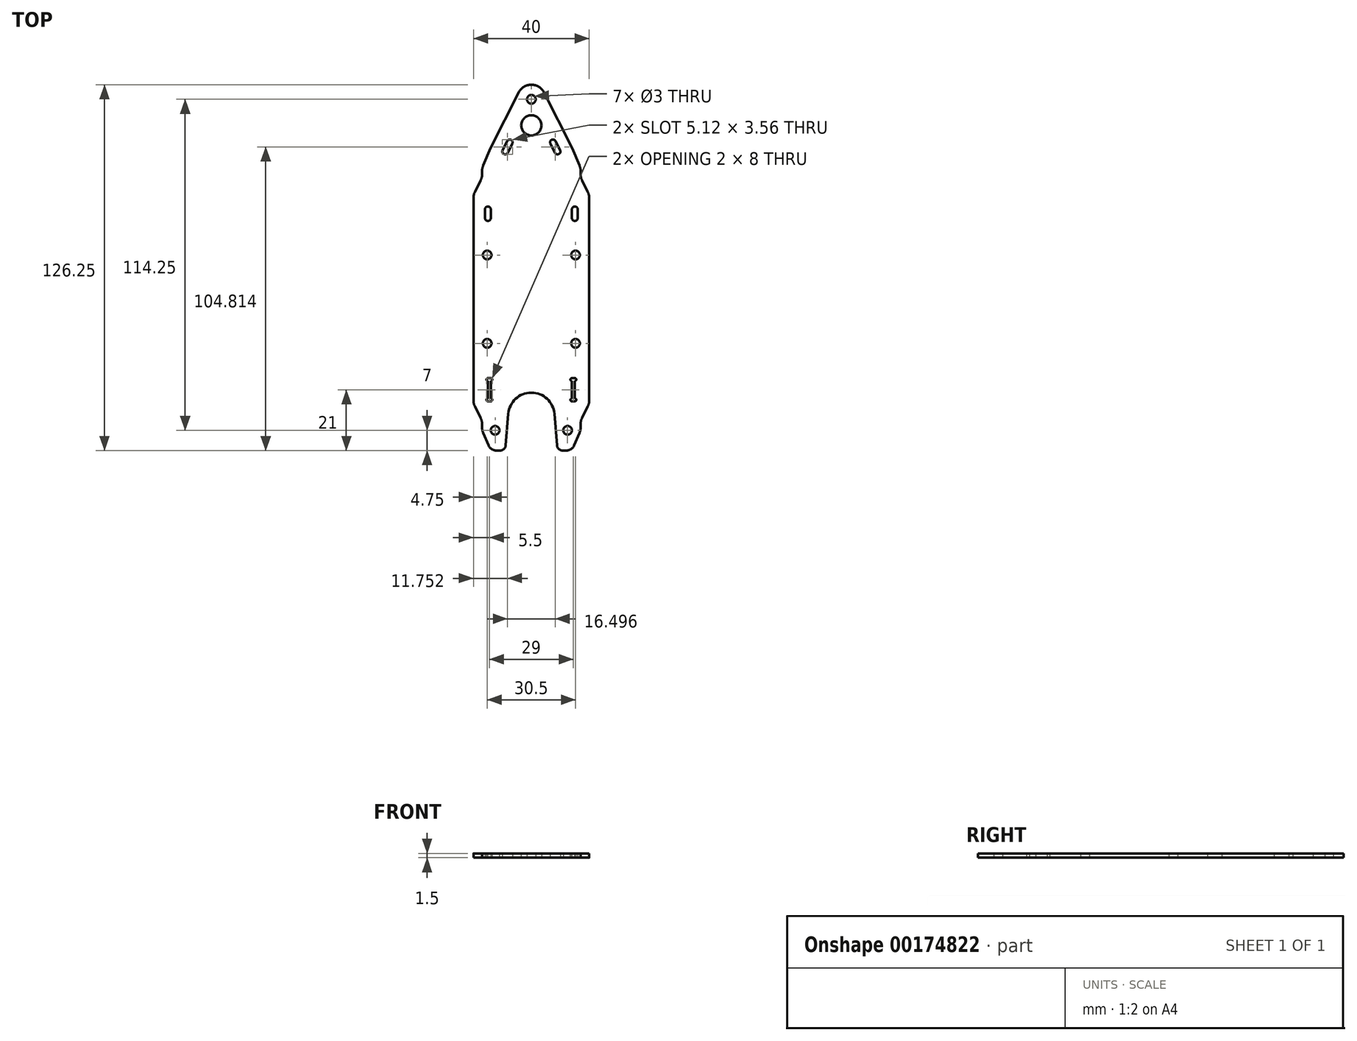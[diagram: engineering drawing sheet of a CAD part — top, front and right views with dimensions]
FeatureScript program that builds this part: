
annotation { "Feature Type Name" : "Feature", "Feature Type Description" : "" }
export const myFeature = defineFeature(function(context is Context, id is Id, definition is map)
    precondition{}
    {
        {
            var Q0;
            Q0=qCreatedBy(makeId("Top.planeOp"),FACE);
            var sketch = newSketch(context, id + "F0", { "sketchPlane" : qUnion([Q0])});
            skLineSegment(sketch, "E0.left", {"start": v(-20, 36) * mm, "end": v(-20, -36) * mm});
            skLineSegment(sketch, "E0.right", {"start": v(20, 36) * mm, "end": v(20, -36) * mm});
            skLineSegment(sketch, "E1.left", {"start": v(-17, 45.25) * mm, "end": v(-17, 42) * mm});
            skLineSegment(sketch, "E1.right", {"start": v(17, 45.25) * mm, "end": v(17, 42) * mm});
            skLineSegment(sketch, "E2.top", {"start": v(-14, -52.25) * mm, "end": v(-9, -52.25) * mm});
            skLineSegment(sketch, "E3", {"start": v(-14, 52.25) * mm, "end": v(-17, 45.25) * mm});
            skLineSegment(sketch, "E4", {"start": v(-20, 36) * mm, "end": v(-17, 42) * mm});
            skLineSegment(sketch, "E5", {"start": v(14, 52.25) * mm, "end": v(17, 45.25) * mm});
            skLineSegment(sketch, "E6", {"start": v(17, 42) * mm, "end": v(20, 36) * mm});
            skLineSegment(sketch, "E7", {"start": v(-14, -52.25) * mm, "end": v(-17, -45.25) * mm});
            skLineSegment(sketch, "E8", {"start": v(-20, -36) * mm, "end": v(-17, -42) * mm});
            skLineSegment(sketch, "E9", {"start": v(20, -36) * mm, "end": v(17, -42) * mm});
            skLineSegment(sketch, "E10", {"start": v(14, -52.25) * mm, "end": v(17, -45.25) * mm});
            skLineSegment(sketch, "E11.trimOffspring", {"start": v(17, -42) * mm, "end": v(17, -45.25) * mm});
            skLineSegment(sketch, "E12.trimOffspring", {"start": v(-17, -42) * mm, "end": v(-17, -45.25) * mm});
            skLineSegment(sketch, "E13.bottom", {"start": v(-15.25, 15.25) * mm, "end": v(15.25, 15.25) * mm, "construction": true});
            skLineSegment(sketch, "E13.top", {"start": v(-15.25, -15.25) * mm, "end": v(15.25, -15.25) * mm, "construction": true});
            skLineSegment(sketch, "E13.left", {"start": v(-15.25, 15.25) * mm, "end": v(-15.25, -15.25) * mm, "construction": true});
            skLineSegment(sketch, "E13.right", {"start": v(15.25, 15.25) * mm, "end": v(15.25, -15.25) * mm, "construction": true});
            skCircle(sketch, "E14", {"center": v(-15.25, 15.25) * mm, "radius": 1.5 * mm});
            skCircle(sketch, "E15", {"center": v(15.25, 15.25) * mm, "radius": 1.5 * mm});
            skCircle(sketch, "E16", {"center": v(15.25, -15.25) * mm, "radius": 1.5 * mm});
            skCircle(sketch, "E17", {"center": v(-15.25, -15.25) * mm, "radius": 1.5 * mm});
            skCircle(sketch, "E18", {"center": v(-12.5, -45.25) * mm, "radius": 1.5 * mm});
            skCircle(sketch, "E19", {"center": v(12.5, -45.25) * mm, "radius": 1.5 * mm});
            skCircle(sketch, "E20", {"center": v(0, 69) * mm, "radius": 1.5 * mm});
            skLineSegment(sketch, "E21", {"start": v(-14, 52.25) * mm, "end": v(-4.47, 71.24) * mm});
            skLineSegment(sketch, "E22", {"start": v(4.47, 71.24) * mm, "end": v(14, 52.25) * mm});
            skPoint(sketch, "E23.visualSharp", {"position": v(0, 80.15) * mm});
            skArc(sketch, "E23.filletArc", {"start": v(4.47, 71.24) * mm, "mid": v(0, 74) * mm, "end": v(-4.47, 71.24) * mm});
            skCircle(sketch, "E24", {"center": v(0, 60) * mm, "radius": 3.5 * mm});
            skArc(sketch, "E25", {"start": v(8.14, 50.55) * mm, "mid": v(9.48, 50.1) * mm, "end": v(9.93, 51.45) * mm});
            skArc(sketch, "E26", {"start": v(8.36, 54.58) * mm, "mid": v(7.01, 55.02) * mm, "end": v(6.57, 53.68) * mm});
            skLineSegment(sketch, "E27", {"start": v(7.46, 54.13) * mm, "end": v(9.03, 51) * mm, "construction": true});
            skLineSegment(sketch, "E28", {"start": v(6.57, 53.68) * mm, "end": v(8.14, 50.55) * mm});
            skLineSegment(sketch, "E29", {"start": v(8.36, 54.58) * mm, "end": v(9.93, 51.45) * mm});
            skArc(sketch, "E30.MirrorCS", {"start": v(-8.14, 50.55) * mm, "mid": v(-9.48, 50.1) * mm, "end": v(-9.93, 51.45) * mm});
            skLineSegment(sketch, "E31.MirrorCS", {"start": v(-7.46, 54.13) * mm, "end": v(-9.03, 51) * mm, "construction": true});
            skLineSegment(sketch, "E32.MirrorCS", {"start": v(-8.36, 54.58) * mm, "end": v(-9.93, 51.45) * mm});
            skLineSegment(sketch, "E33.MirrorCS", {"start": v(-6.57, 53.68) * mm, "end": v(-8.14, 50.55) * mm});
            skArc(sketch, "E34.MirrorCS", {"start": v(-8.36, 54.58) * mm, "mid": v(-7.01, 55.02) * mm, "end": v(-6.57, 53.68) * mm});
            skArc(sketch, "E35", {"start": v(14, 28) * mm, "mid": v(15, 27) * mm, "end": v(16, 28) * mm});
            skArc(sketch, "E36", {"start": v(16, 31) * mm, "mid": v(15, 32) * mm, "end": v(14, 31) * mm});
            skLineSegment(sketch, "E37", {"start": v(15, 31) * mm, "end": v(15, 28) * mm, "construction": true});
            skLineSegment(sketch, "E38", {"start": v(14, 31) * mm, "end": v(14, 28) * mm});
            skLineSegment(sketch, "E39", {"start": v(16, 31) * mm, "end": v(16, 28) * mm});
            skArc(sketch, "E40.MirrorCS", {"start": v(-16, 31) * mm, "mid": v(-15, 32) * mm, "end": v(-14, 31) * mm});
            skLineSegment(sketch, "E41.MirrorCS", {"start": v(-16, 31) * mm, "end": v(-16, 28) * mm});
            skLineSegment(sketch, "E42.MirrorCS", {"start": v(-14, 31) * mm, "end": v(-14, 28) * mm});
            skArc(sketch, "E43.MirrorCS", {"start": v(-14, 28) * mm, "mid": v(-15, 27) * mm, "end": v(-16, 28) * mm});
            skLineSegment(sketch, "E44.MirrorCS", {"start": v(-15, 31) * mm, "end": v(-15, 28) * mm, "construction": true});
            skArc(sketch, "E45", {"start": v(7.97, -39.6) * mm, "mid": v(0, -32.25) * mm, "end": v(-7.97, -39.6) * mm});
            skLineSegment(sketch, "E46", {"start": v(-7.97, -39.6) * mm, "end": v(-9, -52.25) * mm});
            skLineSegment(sketch, "E47", {"start": v(7.97, -39.6) * mm, "end": v(9, -52.25) * mm});
            skLineSegment(sketch, "E48.trimOffspring", {"start": v(9, -52.25) * mm, "end": v(14, -52.25) * mm});
            skSolve(sketch);
        }
        {
            var Q0;
            Q0 = qSketchRegion(id + "F0", true);
            extrude(context, id + "F1", {"entities" : qUnion([Q0]), "depth" : 1.5 * mm});
        }
        {
            var Q0;
            Q0=makeQuery(id+"F1.opExtrude","SWEPT_EDGE",EDGE,{"disambiguationData":[OSD([sQuery(id+"F0.wireOp",EDGE,"E10"),sQuery(id+"F0.wireOp",EDGE,"E11.trimOffspring")])]});
            var Q1;
            Q1=makeQuery(id+"F1.opExtrude","SWEPT_EDGE",EDGE,{"disambiguationData":[OSD([sQuery(id+"F0.wireOp",EDGE,"E1.left"),sQuery(id+"F0.wireOp",EDGE,"E4")])]});
            var Q2;
            Q2=makeQuery(id+"F1.opExtrude","SWEPT_EDGE",EDGE,{"disambiguationData":[OSD([sQuery(id+"F0.wireOp",EDGE,"E0.left"),sQuery(id+"F0.wireOp",EDGE,"E4")])]});
            var Q3;
            Q3=makeQuery(id+"F1.opExtrude","SWEPT_EDGE",EDGE,{"disambiguationData":[OSD([sQuery(id+"F0.wireOp",EDGE,"E1.left"),sQuery(id+"F0.wireOp",EDGE,"E3")])]});
            var Q4;
            Q4=makeQuery(id+"F1.opExtrude","SWEPT_EDGE",EDGE,{"disambiguationData":[OSD([sQuery(id+"F0.wireOp",EDGE,"E3"),sQuery(id+"F0.wireOp",EDGE,"E21")])]});
            var Q5;
            Q5=makeQuery(id+"F1.opExtrude","SWEPT_EDGE",EDGE,{"disambiguationData":[OSD([sQuery(id+"F0.wireOp",EDGE,"E5"),sQuery(id+"F0.wireOp",EDGE,"E22")])]});
            var Q6;
            Q6=makeQuery(id+"F1.opExtrude","SWEPT_EDGE",EDGE,{"disambiguationData":[OSD([sQuery(id+"F0.wireOp",EDGE,"E1.right"),sQuery(id+"F0.wireOp",EDGE,"E5")])]});
            var Q7;
            Q7=makeQuery(id+"F1.opExtrude","SWEPT_EDGE",EDGE,{"disambiguationData":[OSD([sQuery(id+"F0.wireOp",EDGE,"E1.right"),sQuery(id+"F0.wireOp",EDGE,"E6")])]});
            var Q8;
            Q8=makeQuery(id+"F1.opExtrude","SWEPT_EDGE",EDGE,{"disambiguationData":[OSD([sQuery(id+"F0.wireOp",EDGE,"E0.right"),sQuery(id+"F0.wireOp",EDGE,"E6")])]});
            var Q9;
            Q9=makeQuery(id+"F1.opExtrude","SWEPT_EDGE",EDGE,{"disambiguationData":[OSD([sQuery(id+"F0.wireOp",EDGE,"E0.right"),sQuery(id+"F0.wireOp",EDGE,"E9")])]});
            var Q10;
            Q10=makeQuery(id+"F1.opExtrude","SWEPT_EDGE",EDGE,{"disambiguationData":[OSD([sQuery(id+"F0.wireOp",EDGE,"E9"),sQuery(id+"F0.wireOp",EDGE,"E11.trimOffspring")])]});
            var Q11;
            Q11=makeQuery(id+"F1.opExtrude","SWEPT_EDGE",EDGE,{"disambiguationData":[OSD([sQuery(id+"F0.wireOp",EDGE,"E10"),sQuery(id+"F0.wireOp",EDGE,"E11.trimOffspring")])]});
            var Q12;
            Q12=makeQuery(id+"F1.opExtrude","SWEPT_EDGE",EDGE,{"disambiguationData":[OSD([sQuery(id+"F0.wireOp",EDGE,"E8"),sQuery(id+"F0.wireOp",EDGE,"E12.trimOffspring")])]});
            var Q13;
            Q13=makeQuery(id+"F1.opExtrude","SWEPT_EDGE",EDGE,{"disambiguationData":[OSD([sQuery(id+"F0.wireOp",EDGE,"E0.left"),sQuery(id+"F0.wireOp",EDGE,"E8")])]});
            var Q14;
            Q14=makeQuery(id+"F1.opExtrude","SWEPT_EDGE",EDGE,{"disambiguationData":[OSD([sQuery(id+"F0.wireOp",EDGE,"E7"),sQuery(id+"F0.wireOp",EDGE,"E12.trimOffspring")])]});
            fillet(context, id + "F2", {"entities" : qUnion([Q0, Q1, Q2, Q3, Q4, Q5, Q6, Q7, Q8, Q9, Q10, Q11, Q12, Q13, Q14]), "radius" : 5 * mm, "tangentPropagation" : true, "allowEdgeOverflow" : false});
        }
        {
            var Q0;
            Q0=makeQuery(id+"F1.opExtrude","CAP_FACE",FACE,{"disambiguationData":[OSD([sQuery(id+"F0.wireOp",EDGE,"E0.left"),sQuery(id+"F0.wireOp",EDGE,"E0.right"),sQuery(id+"F0.wireOp",EDGE,"E1.left"),sQuery(id+"F0.wireOp",EDGE,"E1.right"),sQuery(id+"F0.wireOp",EDGE,"E2.top"),sQuery(id+"F0.wireOp",EDGE,"E3"),sQuery(id+"F0.wireOp",EDGE,"E4"),sQuery(id+"F0.wireOp",EDGE,"E5"),sQuery(id+"F0.wireOp",EDGE,"E6"),sQuery(id+"F0.wireOp",EDGE,"E7"),sQuery(id+"F0.wireOp",EDGE,"E8"),sQuery(id+"F0.wireOp",EDGE,"E9"),sQuery(id+"F0.wireOp",EDGE,"E10"),sQuery(id+"F0.wireOp",EDGE,"E11.trimOffspring"),sQuery(id+"F0.wireOp",EDGE,"E12.trimOffspring"),sQuery(id+"F0.wireOp",EDGE,"E14"),sQuery(id+"F0.wireOp",EDGE,"E15"),sQuery(id+"F0.wireOp",EDGE,"E16"),sQuery(id+"F0.wireOp",EDGE,"E17"),sQuery(id+"F0.wireOp",EDGE,"E18"),sQuery(id+"F0.wireOp",EDGE,"E19"),sQuery(id+"F0.wireOp",EDGE,"E20"),sQuery(id+"F0.wireOp",EDGE,"E21"),sQuery(id+"F0.wireOp",EDGE,"E22"),sQuery(id+"F0.wireOp",EDGE,"E23.filletArc"),sQuery(id+"F0.wireOp",EDGE,"E24"),sQuery(id+"F0.wireOp",EDGE,"E25"),sQuery(id+"F0.wireOp",EDGE,"E26"),sQuery(id+"F0.wireOp",EDGE,"E28"),sQuery(id+"F0.wireOp",EDGE,"E29"),sQuery(id+"F0.wireOp",EDGE,"E30.MirrorCS"),sQuery(id+"F0.wireOp",EDGE,"E32.MirrorCS"),sQuery(id+"F0.wireOp",EDGE,"E33.MirrorCS"),sQuery(id+"F0.wireOp",EDGE,"E34.MirrorCS"),sQuery(id+"F0.wireOp",EDGE,"E35"),sQuery(id+"F0.wireOp",EDGE,"E36"),sQuery(id+"F0.wireOp",EDGE,"E38"),sQuery(id+"F0.wireOp",EDGE,"E39"),sQuery(id+"F0.wireOp",EDGE,"E40.MirrorCS"),sQuery(id+"F0.wireOp",EDGE,"E41.MirrorCS"),sQuery(id+"F0.wireOp",EDGE,"E42.MirrorCS"),sQuery(id+"F0.wireOp",EDGE,"E43.MirrorCS"),sQuery(id+"F0.wireOp",EDGE,"E45"),sQuery(id+"F0.wireOp",EDGE,"E46"),sQuery(id+"F0.wireOp",EDGE,"E47"),sQuery(id+"F0.wireOp",EDGE,"E48.trimOffspring")])],"isStart":false});
            var sketch = newSketch(context, id + "F3", { "sketchPlane" : qUnion([Q0])});
            skLineSegment(sketch, "E49.bottom", {"start": v(-15, -27.25) * mm, "end": v(-14, -27.25) * mm});
            skLineSegment(sketch, "E49.top", {"start": v(-15, -35.25) * mm, "end": v(-14, -35.25) * mm});
            skLineSegment(sketch, "E49.right", {"start": v(-14, -28.25) * mm, "end": v(-14, -34.25) * mm});
            skArc(sketch, "E50", {"start": v(-15, -34.25) * mm, "mid": v(-15.5, -34.75) * mm, "end": v(-15, -35.25) * mm});
            skArc(sketch, "E51", {"start": v(-14, -35.25) * mm, "mid": v(-13.5, -34.75) * mm, "end": v(-14, -34.25) * mm});
            skArc(sketch, "E52", {"start": v(-14, -28.25) * mm, "mid": v(-13.5, -27.75) * mm, "end": v(-14, -27.25) * mm});
            skArc(sketch, "E53", {"start": v(-15, -27.25) * mm, "mid": v(-15.5, -27.75) * mm, "end": v(-15, -28.25) * mm});
            skLineSegment(sketch, "E54.trimOffspring", {"start": v(-15, -28.25) * mm, "end": v(-15, -34.25) * mm});
            skLineSegment(sketch, "E55.MirrorCS", {"start": v(15, -35.25) * mm, "end": v(14, -35.25) * mm});
            skLineSegment(sketch, "E56.MirrorCS", {"start": v(15, -27.25) * mm, "end": v(14, -27.25) * mm});
            skArc(sketch, "E57.MirrorCS", {"start": v(14, -35.25) * mm, "mid": v(13.5, -34.75) * mm, "end": v(14, -34.25) * mm});
            skArc(sketch, "E58.MirrorCS", {"start": v(15, -34.25) * mm, "mid": v(15.5, -34.75) * mm, "end": v(15, -35.25) * mm});
            skArc(sketch, "E59.MirrorCS", {"start": v(14, -28.25) * mm, "mid": v(13.5, -27.75) * mm, "end": v(14, -27.25) * mm});
            skArc(sketch, "E60.MirrorCS", {"start": v(15, -27.25) * mm, "mid": v(15.5, -27.75) * mm, "end": v(15, -28.25) * mm});
            skLineSegment(sketch, "E61.MirrorCS", {"start": v(15, -28.25) * mm, "end": v(15, -34.25) * mm});
            skLineSegment(sketch, "E62.MirrorCS", {"start": v(14, -28.25) * mm, "end": v(14, -34.25) * mm});
            skSolve(sketch);
        }
        {
            var Q0;
            Q0 = qSketchRegion(id + "F3", true);
            extrude(context, id + "F4", {"entities" : qUnion([Q0]), "operationType" : NewBodyOperationType.REMOVE, "oppositeDirection" : true, "depth" : 25 * mm});
        }
        {
            var Q0;
            Q0=makeQuery(id+"F1.opExtrude","SWEPT_EDGE",EDGE,{"disambiguationData":[OSD([sQuery(id+"F0.wireOp",EDGE,"E2.top"),sQuery(id+"F0.wireOp",EDGE,"E46")])]});
            var Q1;
            Q1=makeQuery(id+"F1.opExtrude","SWEPT_EDGE",EDGE,{"disambiguationData":[OSD([sQuery(id+"F0.wireOp",EDGE,"E47"),sQuery(id+"F0.wireOp",EDGE,"E48.trimOffspring")])]});
            fillet(context, id + "F5", {"entities" : qUnion([Q0, Q1]), "radius" : 2 * mm, "tangentPropagation" : true, "allowEdgeOverflow" : false});
        }
        {
            var Q0;
            Q0=makeQuery(id+"F1.opExtrude","SWEPT_EDGE",EDGE,{"disambiguationData":[OSD([sQuery(id+"F0.wireOp",EDGE,"E2.top"),sQuery(id+"F0.wireOp",EDGE,"E7")])]});
            var Q1;
            Q1=makeQuery(id+"F1.opExtrude","SWEPT_EDGE",EDGE,{"disambiguationData":[OSD([sQuery(id+"F0.wireOp",EDGE,"E10"),sQuery(id+"F0.wireOp",EDGE,"E48.trimOffspring")])]});
            fillet(context, id + "F6", {"entities" : qUnion([Q0, Q1]), "radius" : 3 * mm, "tangentPropagation" : true, "allowEdgeOverflow" : false});
        }
    });
